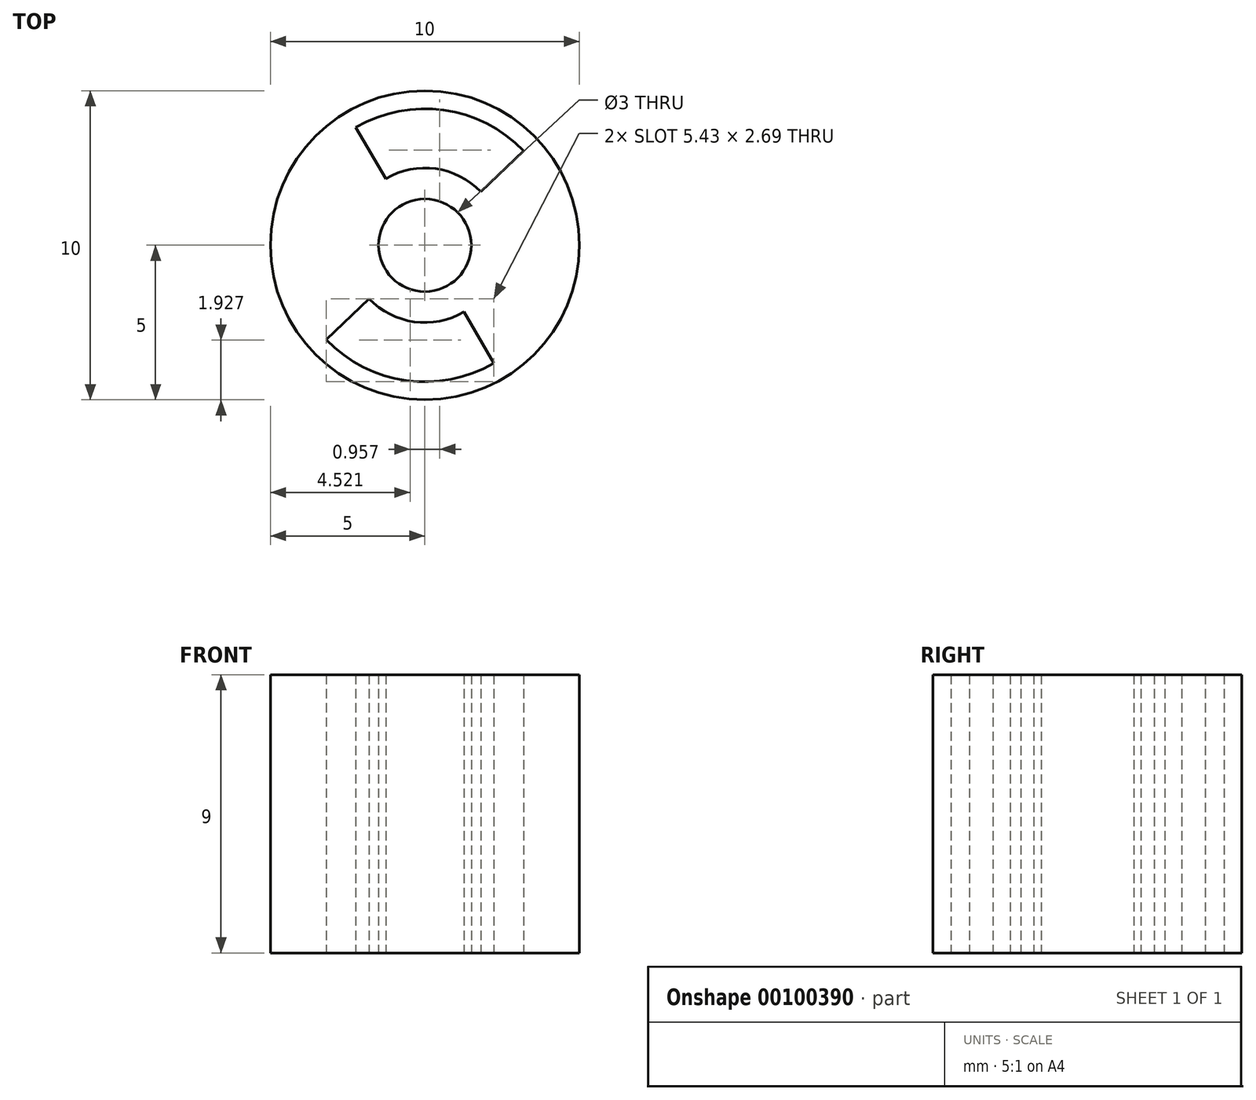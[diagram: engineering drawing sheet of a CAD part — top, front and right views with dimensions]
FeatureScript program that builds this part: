
annotation { "Feature Type Name" : "Feature", "Feature Type Description" : "" }
export const myFeature = defineFeature(function(context is Context, id is Id, definition is map)
    precondition{}
    {
        {
            var Q0;
            Q0=qCreatedBy(makeId("Top.planeOp"),FACE);
            var sketch = newSketch(context, id + "F0", { "sketchPlane" : qUnion([Q0])});
            skCircle(sketch, "E0", {"center": v(0, 0) * mm, "radius": 5 * mm});
            skCircle(sketch, "E1", {"center": v(0, 0) * mm, "radius": 1.5 * mm});
            skArc(sketch, "E2", {"start": v(3.2, 3.06) * mm, "mid": v(0.6, 4.38) * mm, "end": v(-2.23, 3.81) * mm});
            skArc(sketch, "E3", {"start": v(1.8, 1.73) * mm, "mid": v(0.35, 2.48) * mm, "end": v(-1.26, 2.16) * mm});
            skLineSegment(sketch, "E4", {"start": v(-2.23, 3.81) * mm, "end": v(-1.26, 2.16) * mm});
            skLineSegment(sketch, "E5", {"start": v(1.26, -2.16) * mm, "end": v(2.23, -3.81) * mm});
            skLineSegment(sketch, "E6", {"start": v(3.2, 3.06) * mm, "end": v(1.8, 1.73) * mm});
            skLineSegment(sketch, "E7", {"start": v(-1.8, -1.73) * mm, "end": v(-3.2, -3.06) * mm});
            skArc(sketch, "E8.trimOffspring", {"start": v(-1.8, -1.73) * mm, "mid": v(-0.35, -2.48) * mm, "end": v(1.26, -2.16) * mm});
            skArc(sketch, "E9.trimOffspring", {"start": v(-3.2, -3.06) * mm, "mid": v(-0.6, -4.38) * mm, "end": v(2.23, -3.81) * mm});
            skSolve(sketch);
        }
        {
            var Q0;
            Q0=makeQuery(id+"F0.imprint","IMPRINT",FACE,{"disambiguationData":[TD([[makeQuery(id+"F0.imprint","IMPRINT",EDGE,{"derivedFrom":sQuery(id+"F0.wireOp",EDGE,"E0")}),1.0]])]});
            var Q1;
            {var subQ5=sQuery(id+"F0.wireOp",EDGE,"MUWhRQee-nWtj-8YlV-Th1x-MPv9Wnnc0OdF.top");Q1=makeQuery(id+"F0.imprint","IMPRINT",FACE,{"disambiguationData":[TD([[makeQuery(id+"F0.imprint","IMPRINT",EDGE,{"derivedFrom":subQ5}),-1.0]])]});}
            extrude(context, id + "F1", {"entities" : qUnion([Q0, Q1]), "depth" : 9 * mm});
        }
    });
